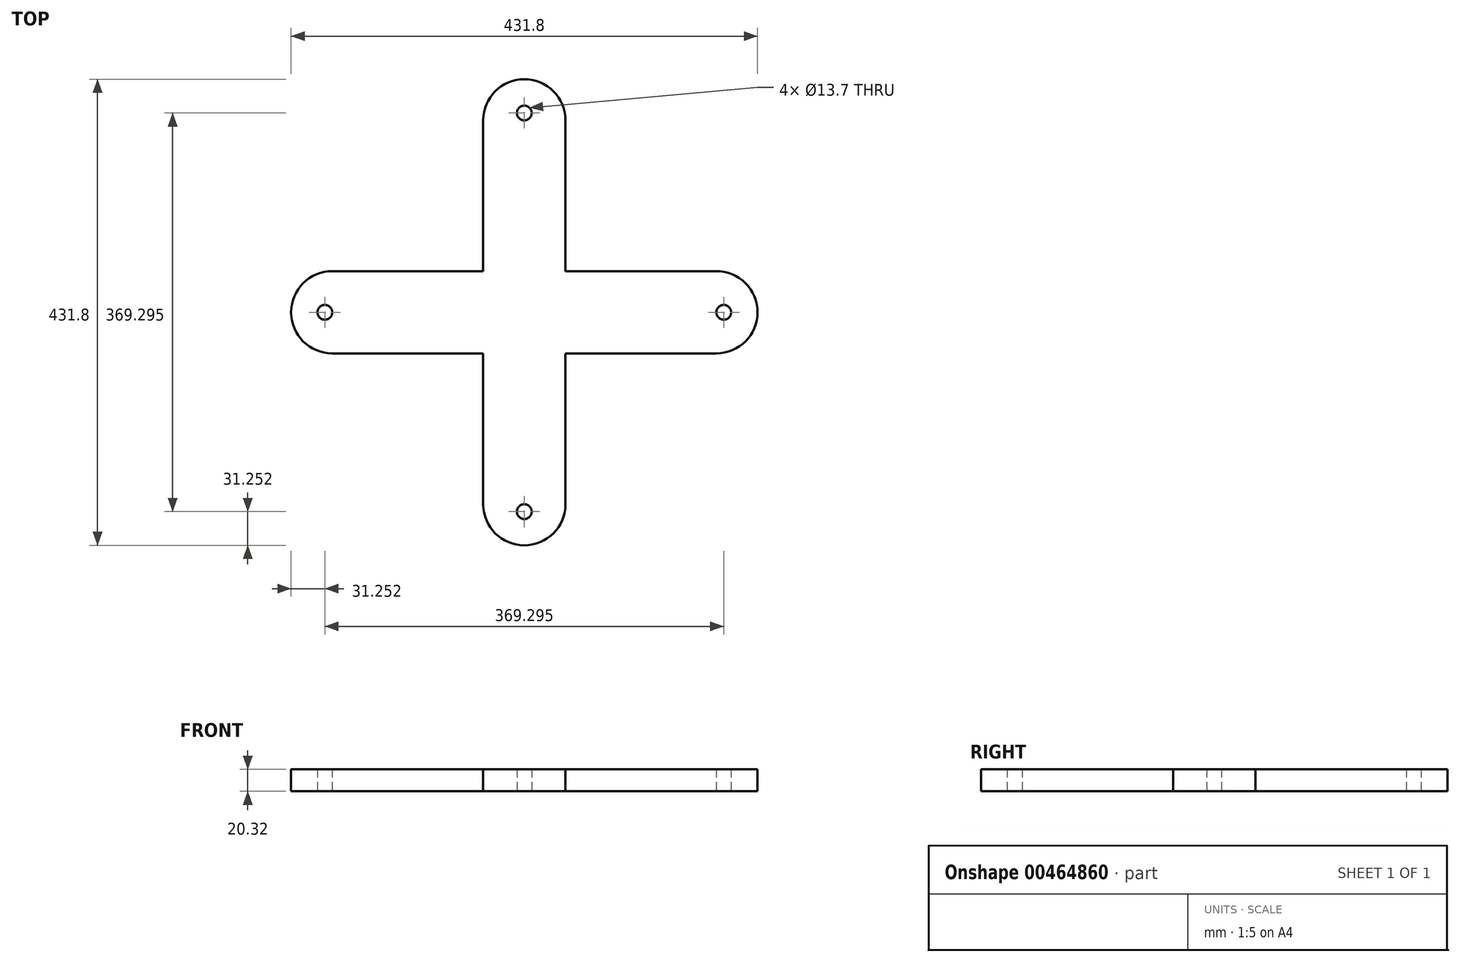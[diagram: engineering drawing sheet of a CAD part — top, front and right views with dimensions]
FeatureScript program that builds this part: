
annotation { "Feature Type Name" : "Feature", "Feature Type Description" : "" }
export const myFeature = defineFeature(function(context is Context, id is Id, definition is map)
    precondition{}
    {
        {
            var Q0;
            Q0=qCreatedBy(makeId("Top.planeOp"),FACE);
            var sketch = newSketch(context, id + "F0", { "sketchPlane" : qUnion([Q0])});
            skLineSegment(sketch, "E0.bottom", {"start": v(0, 0) * mm, "end": v(76.2, 0) * mm});
            skLineSegment(sketch, "E0.top", {"start": v(0, 177.8) * mm, "end": v(76.2, 177.8) * mm});
            skLineSegment(sketch, "E0.left", {"start": v(0, 0) * mm, "end": v(0, 177.8) * mm});
            skLineSegment(sketch, "E0.right", {"start": v(76.2, 0) * mm, "end": v(76.2, 177.8) * mm});
            skArc(sketch, "E1", {"start": v(76.2, 177.8) * mm, "mid": v(38.1, 215.9) * mm, "end": v(0, 177.8) * mm});
            skLineSegment(sketch, "E2.1.0", {"start": v(38.1, 38.1) * mm, "end": v(-139.7, 38.1) * mm});
            skLineSegment(sketch, "E2.1.1", {"start": v(38.1, -38.1) * mm, "end": v(-139.7, -38.1) * mm});
            skArc(sketch, "E2.1.2", {"start": v(-139.7, 38.1) * mm, "mid": v(-177.8, 0) * mm, "end": v(-139.7, -38.1) * mm});
            skLineSegment(sketch, "E2.1.3", {"start": v(-139.7, -38.1) * mm, "end": v(-139.7, 38.1) * mm});
            skLineSegment(sketch, "E2.1.4", {"start": v(38.1, -38.1) * mm, "end": v(38.1, 38.1) * mm});
            skLineSegment(sketch, "E2.2.0", {"start": v(0, 0) * mm, "end": v(0, -177.8) * mm});
            skLineSegment(sketch, "E2.2.1", {"start": v(76.2, 0) * mm, "end": v(76.2, -177.8) * mm});
            skArc(sketch, "E2.2.2", {"start": v(0, -177.8) * mm, "mid": v(38.1, -215.9) * mm, "end": v(76.2, -177.8) * mm});
            skLineSegment(sketch, "E2.2.3", {"start": v(76.2, -177.8) * mm, "end": v(0, -177.8) * mm});
            skLineSegment(sketch, "E2.2.4", {"start": v(76.2, 0) * mm, "end": v(0, 0) * mm});
            skLineSegment(sketch, "E2.3.0", {"start": v(38.1, -38.1) * mm, "end": v(215.9, -38.1) * mm});
            skLineSegment(sketch, "E2.3.1", {"start": v(38.1, 38.1) * mm, "end": v(215.9, 38.1) * mm});
            skArc(sketch, "E2.3.2", {"start": v(215.9, -38.1) * mm, "mid": v(254, 0) * mm, "end": v(215.9, 38.1) * mm});
            skLineSegment(sketch, "E2.3.3", {"start": v(215.9, 38.1) * mm, "end": v(215.9, -38.1) * mm});
            skLineSegment(sketch, "E2.3.4", {"start": v(38.1, 38.1) * mm, "end": v(38.1, -38.1) * mm});
            skPoint(sketch, "E2.center", {"position": v(38.1, 0) * mm});
            skCircle(sketch, "E3", {"center": v(38.1, 184.65) * mm, "radius": 6.85 * mm});
            skCircle(sketch, "E4.1.0", {"center": v(-146.55, 0) * mm, "radius": 6.85 * mm});
            skCircle(sketch, "E4.2.0", {"center": v(38.1, -184.65) * mm, "radius": 6.85 * mm});
            skCircle(sketch, "E4.3.0", {"center": v(222.75, 0) * mm, "radius": 6.85 * mm});
            skSolve(sketch);
        }
        {
            var Q0;
            Q0=makeQuery(id+"F0.imprint","IMPRINT",FACE,{"disambiguationData":[TD([[makeQuery(id+"F0.imprint","IMPRINT",EDGE,{"derivedFrom":sQuery(id+"F0.wireOp",EDGE,"E0.top")}),1.0]])]});
            var Q1;
            Q1=makeQuery(id+"F0.imprint","IMPRINT",FACE,{"disambiguationData":[TD([[makeQuery(id+"F0.imprint","IMPRINT",EDGE,{"derivedFrom":sQuery(id+"F0.wireOp",EDGE,"E2.2.2")}),1.0]])]});
            var Q2;
            Q2=makeQuery(id+"F0.imprint","IMPRINT",FACE,{"disambiguationData":[TD([[makeQuery(id+"F0.imprint","IMPRINT",EDGE,{"derivedFrom":sQuery(id+"F0.wireOp",EDGE,"E2.3.2")}),1.0]])]});
            var Q3;
            {var subQ7=sQuery(id+"F0.wireOp",EDGE,"E0.top");Q3=makeQuery(id+"F0.imprint","IMPRINT",FACE,{"disambiguationData":[TD([[makeQuery(id+"F0.imprint","IMPRINT",EDGE,{"derivedFrom":subQ7}),-1.0]])]});}
            var Q4;
            {var subQ0=sQuery(id+"F0.wireOp",EDGE,"E2.3.3");Q4=makeQuery(id+"F0.imprint","IMPRINT",FACE,{"disambiguationData":[TD([[makeQuery(id+"F0.imprint","IMPRINT",EDGE,{"derivedFrom":subQ0}),-1.0]])]});}
            var Q5;
            {var subQ0=sQuery(id+"F0.wireOp",EDGE,"E2.2.3");Q5=makeQuery(id+"F0.imprint","IMPRINT",FACE,{"disambiguationData":[TD([[makeQuery(id+"F0.imprint","IMPRINT",EDGE,{"derivedFrom":subQ0}),-1.0]])]});}
            var Q6;
            {var subQ1=sQuery(id+"F0.wireOp",EDGE,"E0.left");var subQ3=sQuery(id+"F0.wireOp",EDGE,"E2.1.0");var subQ4=makeQuery(id+"F0.imprint","INTERSECT",VERTEX,{"derivedFrom":[subQ1,subQ3]});Q6=makeQuery(id+"F0.imprint","IMPRINT",FACE,{"disambiguationData":[TD([[makeQuery(id+"F0.imprint","IMPRINT",EDGE,{"disambiguationData":[TD([[subQ4,1.0]])],"derivedFrom":subQ1}),-1.0]])]});}
            var Q7;
            {var subQ1=sQuery(id+"F0.wireOp",EDGE,"E0.right");var subQ3=sQuery(id+"F0.wireOp",EDGE,"E2.3.1");var subQ4=makeQuery(id+"F0.imprint","INTERSECT",VERTEX,{"derivedFrom":[subQ1,subQ3]});Q7=makeQuery(id+"F0.imprint","IMPRINT",FACE,{"disambiguationData":[TD([[makeQuery(id+"F0.imprint","IMPRINT",EDGE,{"disambiguationData":[TD([[subQ4,1.0]])],"derivedFrom":subQ1}),1.0]])]});}
            var Q8;
            {var subQ1=sQuery(id+"F0.wireOp",EDGE,"E2.1.1");var subQ3=sQuery(id+"F0.wireOp",EDGE,"E2.2.0");var subQ4=makeQuery(id+"F0.imprint","INTERSECT",VERTEX,{"derivedFrom":[subQ1,subQ3]});Q8=makeQuery(id+"F0.imprint","IMPRINT",FACE,{"disambiguationData":[TD([[makeQuery(id+"F0.imprint","IMPRINT",EDGE,{"disambiguationData":[TD([[subQ4,1.0]])],"derivedFrom":subQ1}),-1.0]])]});}
            var Q9;
            {var subQ1=sQuery(id+"F0.wireOp",EDGE,"E2.2.1");var subQ3=sQuery(id+"F0.wireOp",EDGE,"E2.3.0");var subQ4=makeQuery(id+"F0.imprint","INTERSECT",VERTEX,{"derivedFrom":[subQ1,subQ3]});Q9=makeQuery(id+"F0.imprint","IMPRINT",FACE,{"disambiguationData":[TD([[makeQuery(id+"F0.imprint","IMPRINT",EDGE,{"disambiguationData":[TD([[subQ4,1.0]])],"derivedFrom":subQ1}),-1.0]])]});}
            var Q10;
            Q10=makeQuery(id+"F0.imprint","IMPRINT",FACE,{"disambiguationData":[TD([[makeQuery(id+"F0.imprint","IMPRINT",EDGE,{"derivedFrom":sQuery(id+"F0.wireOp",EDGE,"E2.1.2")}),1.0]])]});
            var Q11;
            {var subQ0=sQuery(id+"F0.wireOp",EDGE,"E2.1.3");Q11=makeQuery(id+"F0.imprint","IMPRINT",FACE,{"disambiguationData":[TD([[makeQuery(id+"F0.imprint","IMPRINT",EDGE,{"derivedFrom":subQ0}),-1.0]])]});}
            extrude(context, id + "F1", {"entities" : qUnion([Q0, Q1, Q2, Q3, Q4, Q5, Q6, Q7, Q8, Q9, Q10, Q11]), "depth" : 20.32 * mm});
        }
    });
